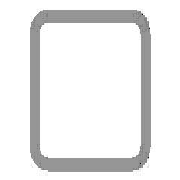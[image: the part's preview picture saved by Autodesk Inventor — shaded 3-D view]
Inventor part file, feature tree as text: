
AUTODESK INVENTOR PART (.ipt)
format: ipt  version: 2024 (Build 280153000, 153)  size: 129,536 bytes
history: native  units: mm (DEFAULTED — no unit token found)
features: other x4, extrude x1, sketch x1, plane x1
ambient origin geometry x8: Origin, YZ Plane, XZ Plane, XY Plane, X Axis, Y Axis, Z Axis, Center Point
bodies: Solid1 (feature_tree)
feature tree (7):
  parser-record x1  (decoder bookkeeping rows leaked as tree rows — omitted from the tree; the rows remain in map.json)
  other  "Driven Length"
  other  "Plano inicial"
  other  "Plano final"
  extrude  "Cuerpo"  TaperAngle=0.0deg  [1 undecoded]
  sketch  "Sketch3"  dims[d3=2190.0mm d4=0.0mm d10=50.8mm d11=50.8mm d12=3.175mm d13=-0.0mm d14=2190.0mm d15=25.4mm d16=25.4mm d17=6.35mm d18=90.0deg d19=2190.0mm]
  plane  "Work Plane3"
note: 1 required parameter value undecoded (feature->parameter linkage not recoverable at this tier; creation-order binding heuristic only, values carry confidence <= 0.55)
